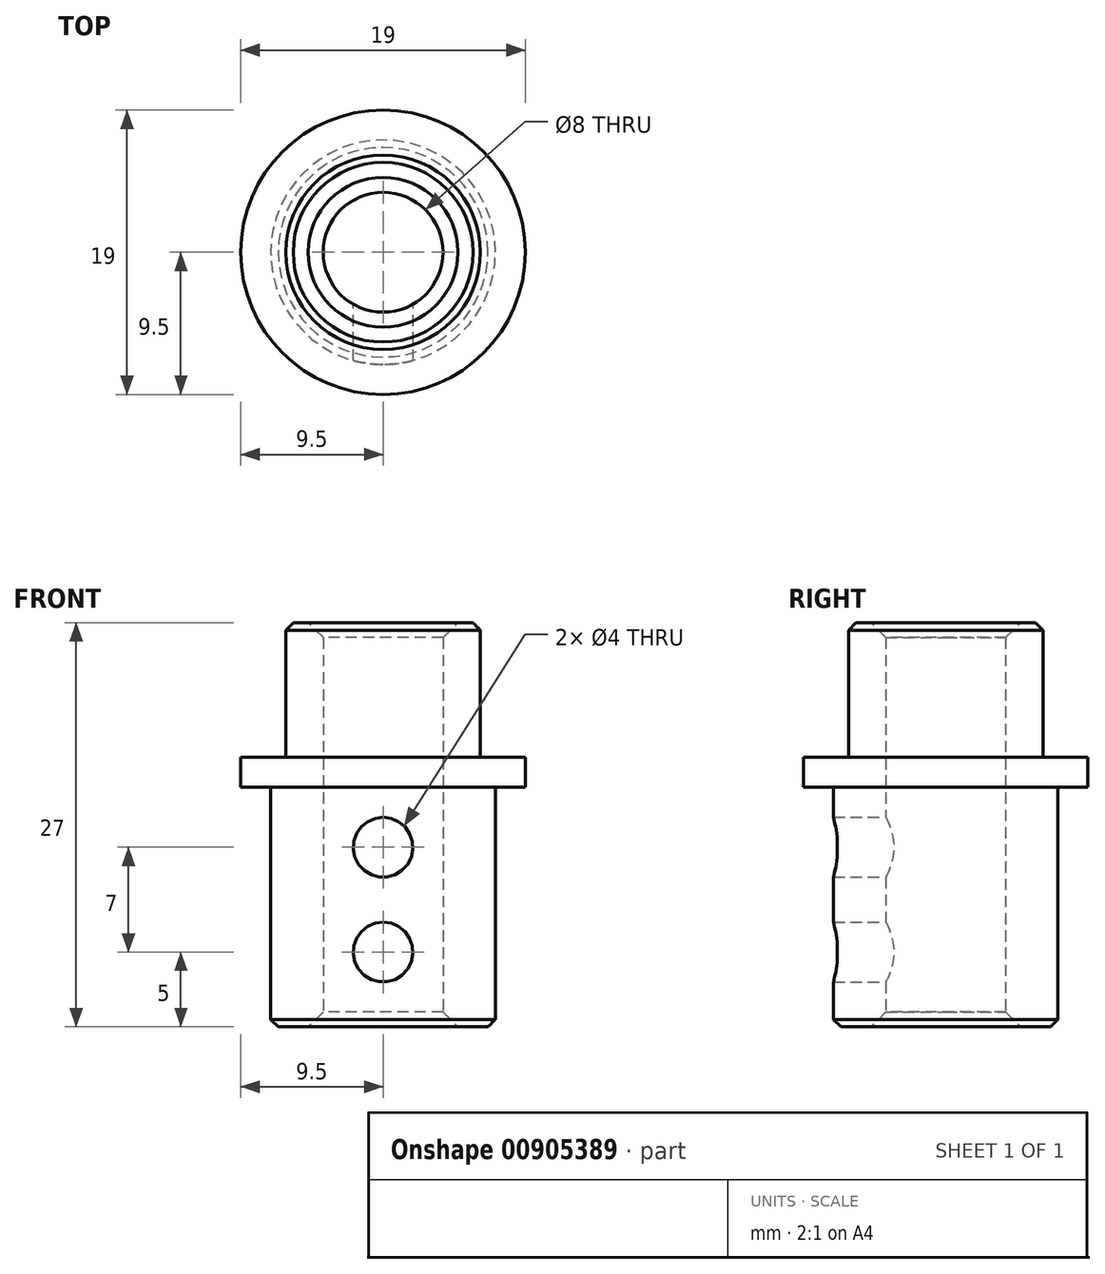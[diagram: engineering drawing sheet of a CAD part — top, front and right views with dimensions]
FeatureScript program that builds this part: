
annotation { "Feature Type Name" : "Feature", "Feature Type Description" : "" }
export const myFeature = defineFeature(function(context is Context, id is Id, definition is map)
    precondition{}
    {
        {
            var Q0;
            Q0=qCreatedBy(makeId("Top.planeOp"),FACE);
            var sketch = newSketch(context, id + "F0", { "sketchPlane" : qUnion([Q0])});
            skCircle(sketch, "E0", {"center": v(0, 0) * mm, "radius": 7.5 * mm});
            skCircle(sketch, "E1", {"center": v(0, 0) * mm, "radius": 4 * mm});
            skSolve(sketch);
        }
        {
            var Q0;
            Q0=makeQuery(id+"F0.imprint","IMPRINT",FACE,{"disambiguationData":[TD([[makeQuery(id+"F0.imprint","IMPRINT",EDGE,{"derivedFrom":sQuery(id+"F0.wireOp",EDGE,"E0")}),1.0]])]});
            extrude(context, id + "F1", {"entities" : qUnion([Q0]), "depth" : 18 * mm, "offsetDistance" : 25 * mm});
        }
        {
            var Q0;
            Q0=makeQuery(id+"F1.opExtrude","CAP_FACE",FACE,{"disambiguationData":[OSD([sQuery(id+"F0.wireOp",EDGE,"E0"),sQuery(id+"F0.wireOp",EDGE,"E1")])],"isStart":false});
            var sketch = newSketch(context, id + "F2", { "sketchPlane" : qUnion([Q0])});
            skCircle(sketch, "E2", {"center": v(0, 0) * mm, "radius": 4 * mm});
            skCircle(sketch, "E3", {"center": v(0, 0) * mm, "radius": 6.5 * mm});
            skSolve(sketch);
        }
        {
            var Q0;
            Q0 = qSketchRegion(id + "F2", true);
            extrude(context, id + "F3", {"entities" : qUnion([Q0]), "operationType" : NewBodyOperationType.ADD, "depth" : 9 * mm, "offsetDistance" : 25 * mm});
        }
        {
            var Q0;
            Q0=makeQuery(id+"F3.opExtrude","CAP_EDGE",EDGE,{"disambiguationData":[OSD([sQuery(id+"F2.wireOp",EDGE,"E2")])],"isStart":false});
            var Q1;
            Q1=makeQuery(id+"F1.opExtrude","CAP_EDGE",EDGE,{"disambiguationData":[OSD([sQuery(id+"F0.wireOp",EDGE,"E1")])],"isStart":true});
            chamfer(context, id + "F4", {"entities" : qUnion([Q0, Q1]), "width" : 1 * mm, "tangentPropagation" : true});
        }
        {
            var Q0;
            Q0=makeQuery(id+"F1.opExtrude","CAP_EDGE",EDGE,{"disambiguationData":[OSD([sQuery(id+"F0.wireOp",EDGE,"E0")])],"isStart":true});
            var Q1;
            Q1=makeQuery(id+"F3.opExtrude","CAP_EDGE",EDGE,{"disambiguationData":[OSD([sQuery(id+"F2.wireOp",EDGE,"E3")])],"isStart":false});
            chamfer(context, id + "F5", {"entities" : qUnion([Q0, Q1]), "width" : .5 * mm, "tangentPropagation" : true});
        }
        {
            var Q0;
            Q0=makeQuery(id+"F1.opExtrude","CAP_FACE",FACE,{"disambiguationData":[OSD([sQuery(id+"F0.wireOp",EDGE,"E0"),sQuery(id+"F0.wireOp",EDGE,"E1")])],"isStart":false});
            var sketch = newSketch(context, id + "F6", { "sketchPlane" : qUnion([Q0])});
            skCircle(sketch, "E4", {"center": v(0, 0) * mm, "radius": 6.5 * mm});
            skCircle(sketch, "E5", {"center": v(0, 0) * mm, "radius": 9.5 * mm});
            skSolve(sketch);
        }
        {
            var Q0;
            Q0 = qSketchRegion(id + "F6", true);
            extrude(context, id + "F7", {"entities" : qUnion([Q0]), "operationType" : NewBodyOperationType.ADD, "oppositeDirection" : true, "depth" : 2 * mm, "offsetDistance" : 25 * mm});
        }
        {
            var Q0;
            Q0=qCreatedBy(makeId("Front.planeOp"),FACE);
            var sketch = newSketch(context, id + "F8", { "sketchPlane" : qUnion([Q0])});
            skCircle(sketch, "E6", {"center": v(0, 5) * mm, "radius": 2 * mm});
            skCircle(sketch, "E7", {"center": v(0, 12) * mm, "radius": 2 * mm});
            skSolve(sketch);
        }
        {
            var Q0;
            Q0 = qSketchRegion(id + "F8", true);
            extrude(context, id + "F9", {"entities" : qUnion([Q0]), "operationType" : NewBodyOperationType.REMOVE, "depth" : 25 * mm, "offsetDistance" : 25 * mm});
        }
    });
